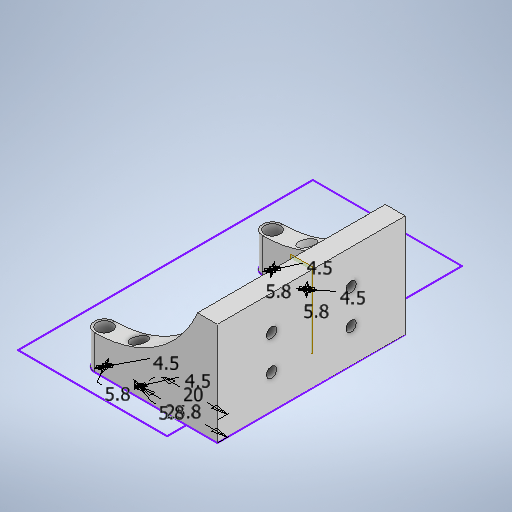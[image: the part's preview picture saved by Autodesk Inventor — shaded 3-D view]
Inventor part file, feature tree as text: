
AUTODESK INVENTOR PART (.ipt)
format: ipt  version: 2025.1 (Build 291241000, 241)  size: 372,224 bytes
history: native  units: in
note: dims shown in document units (in); Inventor stores cm internally (conversion verified against a paired STEP export)
features: extrude x6, sketch x5, projected_geometry x5, plane x1, mirror x1
ambient origin geometry x8: Origin, YZ Plane, XZ Plane, XY Plane, X Axis, Y Axis, Z Axis, Center Point
bodies: Solid1 (feature_tree)
feature tree (18):
  sketch  "Sketch1"  dims[d0=0.2283in d1=0.2283in d2=0.2283in d3=0.2283in d4=0.1772in d5=0.1772in]
  extrude  "Extrusion1"  Depth=0.1772in
  extrude  "Extrusion2"  Depth=0.1772in
  extrude  "Extrusion3"  Depth=0.7874in
  extrude  "Extrusion4"  Depth=0.3937in
  extrude  "Extrusion5"  Depth=0.3937in
  plane  "Work Plane1"
  mirror  "Mirror1"
  extrude  "Extrusion6"  Depth=0.3937in
  sketch  "Sketch2"  dims[d6=0.1772in d7=0.1772in]
  sketch  "Sketch3"  dims[d8=1.0157in d9=0.7874in]
  projected_geometry  "Projected Loop1"
  sketch  "Sketch4"  dims[d10=0.3937in d11=0.0in d12=0.7874in]
  projected_geometry  "Projected Loop2"
  projected_geometry  "Projected Loop3"
  sketch  "Sketch5"  dims[d13=0.3937in d14=0.0in d15=0.2165in d16=0.3937in d17=0.3937in d18=0.2165in d19=0.2165in d20=0.3937in d21=0.2165in d22=1.7008in d23=1.1811in d24=0.126in d25=0.0in d26=0.1181in d27=0.1181in d28=0.1181in d29=0.1181in d30=0.3937in d31=0.0in d32=0.2313in d33=0.0in d34=-0.8504in d35=1.3312in d36=0.0in]
  projected_geometry  "Projected Loop4"
  projected_geometry  "Projected Loop5"
